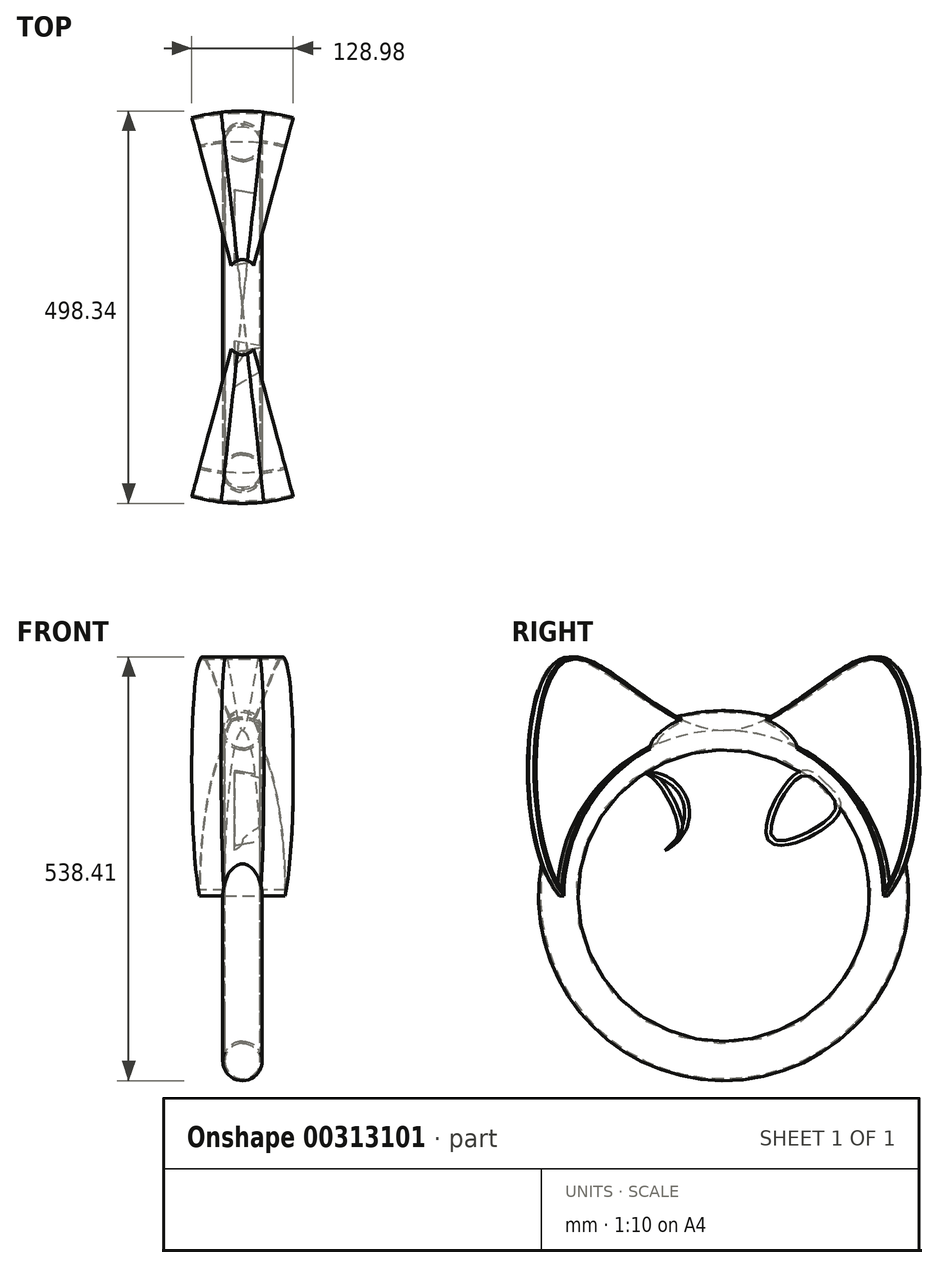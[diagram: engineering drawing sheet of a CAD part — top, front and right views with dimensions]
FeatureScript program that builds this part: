
annotation { "Feature Type Name" : "Feature", "Feature Type Description" : "" }
export const myFeature = defineFeature(function(context is Context, id is Id, definition is map)
    precondition{}
    {
        {
            var Q0;
            Q0=qCreatedBy(makeId("Top.planeOp"),FACE);
            cPlane(context, id + "F0", {"entities" : qUnion([Q0]), "cplaneType" : CPlaneType.OFFSET, "offset" : 57.5 * mm, "width" : 150 * mm, "height" : 150 * mm});
        }
        {
            var Q0;
            Q0=qCreatedBy(id+"F0.planeOp",FACE);
            cPlane(context, id + "F1", {"entities" : qUnion([Q0]), "cplaneType" : CPlaneType.OFFSET, "offset" : 2.5 * mm, "width" : 150 * mm, "height" : 150 * mm});
        }
        {
            var Q0;
            Q0=qCreatedBy(makeId("Top.planeOp"),FACE);
            cPlane(context, id + "F2", {"entities" : qUnion([Q0]), "cplaneType" : CPlaneType.OFFSET, "offset" : 20 * mm, "oppositeDirection" : true, "width" : 150 * mm, "height" : 150 * mm});
        }
        {
            var Q0;
            Q0=qCreatedBy(id+"F2.planeOp",FACE);
            cPlane(context, id + "F3", {"entities" : qUnion([Q0]), "cplaneType" : CPlaneType.OFFSET, "offset" : 20 * mm, "oppositeDirection" : true, "width" : 150 * mm, "height" : 150 * mm});
        }
        {
            var Q0;
            Q0=qCreatedBy(id+"F1.planeOp",FACE);
            cPlane(context, id + "F4", {"entities" : qUnion([Q0]), "cplaneType" : CPlaneType.OFFSET, "offset" : 640 * mm, "width" : 150 * mm, "height" : 150 * mm});
        }
        {
            var Q0;
            Q0=qCreatedBy(id+"F4.planeOp",FACE);
            cPlane(context, id + "F5", {"entities" : qUnion([Q0]), "cplaneType" : CPlaneType.OFFSET, "offset" : 90 * mm, "width" : 150 * mm, "height" : 150 * mm});
        }
        {
            var Q0;
            Q0=qCreatedBy(id+"F3.planeOp",FACE);
            cPlane(context, id + "F6", {"entities" : qUnion([Q0]), "cplaneType" : CPlaneType.OFFSET, "offset" : 150 * mm, "oppositeDirection" : true, "width" : 150 * mm, "height" : 150 * mm});
        }
        {
            var Q0;
            Q0=qCreatedBy(makeId("Top.planeOp"),FACE);
            var sketch = newSketch(context, id + "F7", { "sketchPlane" : qUnion([Q0])});
            skLineSegment(sketch, "E0.bottom", {"start": v(17.5, -7.5) * mm, "end": v(-17.5, -7.5) * mm});
            skLineSegment(sketch, "E0.top", {"start": v(17.5, 7.5) * mm, "end": v(-17.5, 7.5) * mm});
            skLineSegment(sketch, "E0.left", {"start": v(17.5, -7.5) * mm, "end": v(17.5, 7.5) * mm});
            skLineSegment(sketch, "E0.right", {"start": v(-17.5, -7.5) * mm, "end": v(-17.5, 7.5) * mm});
            skPoint(sketch, "E0.middle", {"position": v(0, 0) * mm});
            skSolve(sketch);
        }
        {
            var Q0;
            Q0=qCreatedBy(makeId("Front.planeOp"),FACE);
            var sketch = newSketch(context, id + "F8", { "sketchPlane" : qUnion([Q0])});
            skLineSegment(sketch, "E1", {"start": v(0, 0) * mm, "end": v(0, -210) * mm, "construction": true});
            skCircle(sketch, "E2", {"center": v(0, -210) * mm, "radius": 25 * mm});
            skSolve(sketch);
        }
        {
            var Q0;
            Q0=qCreatedBy(makeId("Right.planeOp"),FACE);
            var sketch = newSketch(context, id + "F9", { "sketchPlane" : qUnion([Q0])});
            skCircle(sketch, "E3", {"center": v(0, 0) * mm, "radius": 210 * mm});
            skFitSpline(sketch, "E4", {"points": [v(0, 0) * mm, v(-210, 0) * mm, v(-210, 300) * mm, v(0, 210) * mm, v(210, 300) * mm, v(210, 0) * mm, v(0, 0) * mm]});
            skLineSegment(sketch, "E5", {"start": v(-210, 0) * mm, "end": v(-210, 300) * mm, "construction": true});
            skLineSegment(sketch, "E6", {"start": v(210, 0) * mm, "end": v(210, 300) * mm, "construction": true});
            skLineSegment(sketch, "E7", {"start": v(0, 0) * mm, "end": v(0, 105) * mm, "construction": true});
            skLineSegment(sketch, "E8", {"start": v(0, 105) * mm, "end": v(-95, 105) * mm, "construction": true});
            skLineSegment(sketch, "E9.MirrorCS", {"start": v(0, 105) * mm, "end": v(95, 105) * mm, "construction": true});
            skCircle(sketch, "E10", {"center": v(-95, 105) * mm, "radius": 50 * mm});
            skPoint(sketch, "E11.1.internal.snap0", {"position": v(-47.5, 105) * mm});
            skPoint(sketch, "E11.3.internal.snap0", {"position": v(-47.5, 105) * mm});
            skLineSegment(sketch, "E12", {"start": v(-59.64, 69.64) * mm, "end": v(-130.36, 140.36) * mm, "construction": true});
            skLineSegment(sketch, "E13", {"start": v(-95, 105) * mm, "end": v(-145, 105) * mm, "construction": true});
            skLineSegment(sketch, "E14", {"start": v(-95, 105) * mm, "end": v(-95, 155) * mm, "construction": true});
            skLineSegment(sketch, "E15", {"start": v(-145, 105) * mm, "end": v(-130.36, 140.36) * mm, "construction": true});
            skLineSegment(sketch, "E16", {"start": v(-130.36, 140.36) * mm, "end": v(-95, 155) * mm, "construction": true});
            skFitSpline(sketch, "E17", {"points": [v(-59.64, 69.64) * mm, v(-95, 155) * mm, v(-130.36, 140.36) * mm, v(-145, 105) * mm, v(-59.64, 69.64) * mm]});
            skFitSpline(sketch, "E18.MirrorC", {"points": [v(59.64, 69.64) * mm, v(95, 155) * mm, v(130.36, 140.36) * mm, v(145, 105) * mm, v(59.64, 69.64) * mm]});
            skSolve(sketch);
        }
        {
            var Q0;
            Q0=makeQuery(id+"F8.imprint","IMPRINT",FACE,{"disambiguationData":[TD([[makeQuery(id+"F8.imprint","IMPRINT",EDGE,{"derivedFrom":sQuery(id+"F8.wireOp",EDGE,"E2")}),1.0]])]});
            var Q1;
            Q1=sQuery(id+"F9.wireOp",EDGE,"E3");
            sweep(context, id + "F10", {"profiles" : qUnion([Q0]), "path" : qUnion([Q1])});
        }
        {
            var Q0;
            {var subQ0=sQuery(id+"F9.wireOp",EDGE,"E17");var subQ1=sQuery(id+"F9.wireOp",EDGE,"E10");var subQ2=makeQuery(id+"F9.imprint","INTERSECT",VERTEX,{"disambiguationData":[OD(0.0)],"derivedFrom":[subQ1,subQ0]});Q0=makeQuery(id+"F9.imprint","IMPRINT",FACE,{"disambiguationData":[TD([[makeQuery(id+"F9.imprint","IMPRINT",EDGE,{"disambiguationData":[TD([[subQ2,1.0]])],"derivedFrom":subQ1}),1.0]])]});}
            var Q1;
            Q1=makeQuery(id+"F9.imprint","IMPRINT",FACE,{"disambiguationData":[TD([[makeQuery(id+"F9.imprint","IMPRINT",EDGE,{"derivedFrom":sQuery(id+"F9.wireOp",EDGE,"E18.MirrorC")}),-1.0]])]});
            extrude(context, id + "F11", {"entities" : qUnion([Q0, Q1]), "depth" : 25 * mm, "hasDraft" : true, "draftAngle" : 10 * degree, "draftPullDirection" : true, "hasSecondDirection" : true, "secondDirectionOppositeDirection" : true, "secondDirectionDepth" : 10 * mm, "hasSecondDirectionDraft" : true, "secondDirectionDraftAngle" : 10 * degree});
        }
        {
            var Q0;
            {var subQ0=sQuery(id+"F9.wireOp",EDGE,"E4");var subQ1=sQuery(id+"F9.wireOp",EDGE,"E3");var subQ2=makeQuery(id+"F9.imprint","INTERSECT",VERTEX,{"disambiguationData":[OD(0.0)],"derivedFrom":[subQ1,subQ0]});Q0=makeQuery(id+"F9.imprint","IMPRINT",FACE,{"disambiguationData":[TD([[makeQuery(id+"F9.imprint","IMPRINT",EDGE,{"disambiguationData":[TD([[subQ2,-1.0]])],"derivedFrom":subQ1}),-1.0]])]});}
            var Q1;
            {var subQ0=sQuery(id+"F9.wireOp",EDGE,"E4");var subQ1=sQuery(id+"F9.wireOp",EDGE,"E3");var subQ2=makeQuery(id+"F9.imprint","INTERSECT",VERTEX,{"disambiguationData":[OD(0.0)],"derivedFrom":[subQ1,subQ0]});Q1=makeQuery(id+"F9.imprint","IMPRINT",FACE,{"disambiguationData":[TD([[makeQuery(id+"F9.imprint","IMPRINT",EDGE,{"disambiguationData":[TD([[subQ2,1.0]])],"derivedFrom":subQ1}),-1.0]])]});}
            var Q2;
            Q2=sQuery(id+"F8.wireOp",EDGE,"E1");
            revolve(context, id + "F12", {"operationType" : NewBodyOperationType.ADD, "entities" : qUnion([Q0, Q1]), "axis" : qUnion([Q2]), "revolveType" : RevolveType.SYMMETRIC, "angle" : 30 * degree});
        }
        {
            var Q0;
            {var subQ0=sQuery(id+"F9.wireOp",EDGE,"E4");var subQ1=sQuery(id+"F9.wireOp",EDGE,"E3");var subQ2=makeQuery(id+"F9.imprint","INTERSECT",VERTEX,{"disambiguationData":[OD(0.0)],"derivedFrom":[subQ1,subQ0]});Q0=makeQuery(id+"F12.opRevolve","CAP_FACE",FACE,{"disambiguationData":[OSD([subQ1,subQ0]),TDD([makeQuery(id+"F9.imprint","IMPRINT",EDGE,{"disambiguationData":[TD([[subQ2,1.0]])],"derivedFrom":subQ1}),makeQuery(id+"F9.imprint","IMPRINT",EDGE,{"disambiguationData":[TD([[subQ2,-1.0]])],"derivedFrom":subQ0})]),OD(0.0)],"isStart":false});}
            var Q1;
            {var subQ0=sQuery(id+"F9.wireOp",EDGE,"E4");var subQ1=sQuery(id+"F9.wireOp",EDGE,"E3");var subQ2=makeQuery(id+"F9.imprint","INTERSECT",VERTEX,{"disambiguationData":[OD(0.0)],"derivedFrom":[subQ1,subQ0]});Q1=makeQuery(id+"F12.opRevolve","CAP_FACE",FACE,{"disambiguationData":[OSD([subQ1,subQ0]),TDD([makeQuery(id+"F9.imprint","IMPRINT",EDGE,{"disambiguationData":[TD([[subQ2,-1.0]])],"derivedFrom":subQ1}),makeQuery(id+"F9.imprint","IMPRINT",EDGE,{"disambiguationData":[TD([[subQ2,1.0]])],"derivedFrom":subQ0})])],"isStart":false});}
            var Q2;
            Q2=makeQuery(id+"F12.opRevolve","CAP_FACE",FACE,{"disambiguationData":[OSD([sQuery(id+"F9.wireOp",EDGE,"E3"),sQuery(id+"F9.wireOp",EDGE,"E4")])],"isStart":true});
            var Q3;
            {var subQ0=sQuery(id+"F9.wireOp",EDGE,"E4");var subQ1=sQuery(id+"F9.wireOp",EDGE,"E3");var subQ2=makeQuery(id+"F9.imprint","INTERSECT",VERTEX,{"disambiguationData":[OD(0.0)],"derivedFrom":[subQ1,subQ0]});Q3=makeQuery(id+"F12.opRevolve","CAP_FACE",FACE,{"disambiguationData":[OSD([subQ1,subQ0]),TDD([makeQuery(id+"F9.imprint","IMPRINT",EDGE,{"disambiguationData":[TD([[subQ2,1.0]])],"derivedFrom":subQ1}),makeQuery(id+"F9.imprint","IMPRINT",EDGE,{"disambiguationData":[TD([[subQ2,-1.0]])],"derivedFrom":subQ0})]),OD(1.0)],"isStart":false});}
            shell(context, id + "F13", {"entities" : qUnion([Q0, Q1, Q2, Q3]), "thickness" : 2.5 * mm});
        }
        {
            var Q0;
            {var subQ0=sQuery(id+"F9.wireOp",EDGE,"E4");var subQ1=sQuery(id+"F9.wireOp",EDGE,"E3");var subQ2=makeQuery(id+"F9.imprint","INTERSECT",VERTEX,{"disambiguationData":[OD(0.0)],"derivedFrom":[subQ1,subQ0]});Q0=makeQuery(id+"F9.imprint","IMPRINT",FACE,{"disambiguationData":[TD([[makeQuery(id+"F9.imprint","IMPRINT",EDGE,{"disambiguationData":[TD([[subQ2,1.0]])],"derivedFrom":subQ1}),-1.0]])]});}
            var Q1;
            {var subQ0=sQuery(id+"F9.wireOp",EDGE,"E4");var subQ1=sQuery(id+"F9.wireOp",EDGE,"E3");var subQ2=makeQuery(id+"F9.imprint","INTERSECT",VERTEX,{"disambiguationData":[OD(0.0)],"derivedFrom":[subQ1,subQ0]});Q1=makeQuery(id+"F9.imprint","IMPRINT",FACE,{"disambiguationData":[TD([[makeQuery(id+"F9.imprint","IMPRINT",EDGE,{"disambiguationData":[TD([[subQ2,-1.0]])],"derivedFrom":subQ1}),-1.0]])]});}
            var Q2;
            Q2=sQuery(id+"F8.wireOp",EDGE,"E1");
            revolve(context, id + "F14", {"entities" : qUnion([Q0, Q1]), "axis" : qUnion([Q2]), "revolveType" : RevolveType.SYMMETRIC, "angle" : 12.5 * degree});
        }
    });
